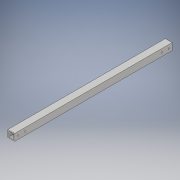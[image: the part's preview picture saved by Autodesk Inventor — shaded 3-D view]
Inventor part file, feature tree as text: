
AUTODESK INVENTOR PART (.ipt)
format: ipt  version: 2018 (Build 220112000, 112)  size: 117,248 bytes
history: native  units: in
note: dims shown in document units (in); Inventor stores cm internally (conversion verified against a paired STEP export)
features: extrude x2, sketch x2
ambient origin geometry x8: Origin, YZ Plane, XZ Plane, XY Plane, X Axis, Y Axis, Z Axis, Center Point
bodies: Solid1 (feature_tree)
feature tree (4):
  extrude  "Extrusion1"  Depth=1.0in
  extrude  "Extrusion2"  Depth=23.0in TaperAngle=0.0deg
  sketch  "Sketch1"  dims[d0=1.0in d1=1.0in]
  sketch  "Sketch2"  dims[d2=0.125in d3=23.0in d4=0.0in d5=0.5in d6=1.0in d7=0.5in d8=1.0in d9=0.2031in d10=23.0in d11=0.0in]
